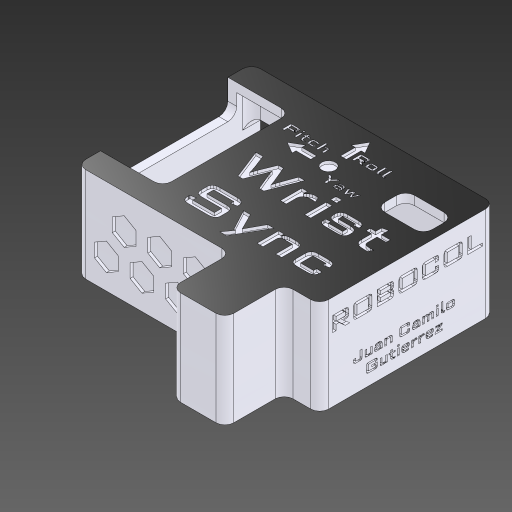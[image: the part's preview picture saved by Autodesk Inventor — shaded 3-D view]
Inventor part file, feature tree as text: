
AUTODESK INVENTOR PART (.ipt)
format: ipt  version: 2023.3 (Build 273359000, 359)  size: 2,437,120 bytes
history: native  units: mm
features: sketch x25, extrude x24, fillet x5, projected_geometry x3, other x2, plane x1, hole x1
ambient origin geometry x8: Origin, YZ Plane, XZ Plane, XY Plane, X Axis, Y Axis, Z Axis, Center Point
bodies: Solid1 (feature_tree)
feature tree (61):
  extrude  "Extrusion1"  Depth=60.0mm
  sketch  "Sketch2"  dims[d2=15.0mm d3=0.0mm d4=8.0mm]
  plane  "Work Plane1"
  extrude  "Extrusion2"  Depth=15.0mm
  extrude  "Extrusion3"  Depth=5.0mm
  extrude  "Extrusion4"  Depth=5.0mm
  extrude  "Extrusion5"  Depth=15.0mm
  extrude  "Extrusion6"  Depth=25.0mm
  extrude  "Extrusion7"  Depth=20.0mm
  extrude  "Extrusion8"  Depth=5.0mm
  hole  "Hole1"  [1 undecoded]
  extrude  "Extrusion9"  Depth=36.0mm
  extrude  "Extrusion10"  Depth=3.0mm TaperAngle=0.0deg
  extrude  "Extrusion11"  Depth=4.0mm
  extrude  "Extrusion12"  Depth=3.0mm TaperAngle=0.0deg
  extrude  "Extrusion13"  Depth=5.0mm
  extrude  "Extrusion14"  Depth=5.0mm
  extrude  "Extrusion15"  Depth=3.0mm TaperAngle=0.0deg
  extrude  "Extrusion16"  Depth=6.0mm
  extrude  "Extrusion17"  Depth=3.0mm TaperAngle=0.0deg
  fillet  "Fillet1"  Radius=12.0mm
  fillet  "Fillet2"  Radius=3.0mm
  fillet  "Fillet3"  Radius=17.0mm
  fillet  "Fillet4"  Radius=3.0mm
  fillet  "Fillet5"  Radius=3.0mm
  extrude  "Extrusion18"  Depth=9.0mm TaperAngle=0.0deg
  extrude  "Extrusion19"  Depth=5.0mm
  extrude  "Extrusion20"  Depth=10.0mm TaperAngle=0.0deg
  extrude  "Extrusion21"  Depth=10.0mm
  extrude  "Extrusion22"  Depth=10.0mm
  extrude  "Extrusion23"  Depth=5.0mm
  extrude  "Extrusion24"  Depth=3.0mm TaperAngle=0.0deg
  sketch  "Sketch1"  dims[d0=60.0mm d1=40.0mm]
  other  "Case"
  sketch  "Sketch3"  dims[d5=5.0mm d6=8.0mm]
  sketch  "Sketch4"  dims[d7=8.0mm d8=3.0mm d9=0.0mm d10=5.0mm]
  sketch  "Sketch5"  dims[d11=10.0mm d12=15.0mm]
  sketch  "Sketch6"  dims[d13=3.0mm d14=0.0mm d15=25.0mm]
  sketch  "Sketch7"  dims[d16=20.0mm d17=9.0mm]
  sketch  "Sketch8"  dims[d18=5.0mm d19=0.0mm d20=8.0mm]
  sketch  "Sketch9"  dims[d21=3.0mm d22=0.0mm d23=3.0mm]
  sketch  "Sketch10"  dims[d24=4.0mm d25=36.0mm]
  sketch  "Sketch11"  dims[d26=1.5mm d27=3.0mm d28=0.0mm]
  sketch  "Sketch12"  dims[d30=9.5mm d31=4.0mm]
  sketch  "Sketch13"  dims[d32=3.0mm d33=0.0mm d34=3.0mm d35=0.0mm]
  projected_geometry  "Projected Loop1"
  sketch  "Sketch14"  dims[d36=5.0mm d37=5.0mm]
  projected_geometry  "Projected Loop2"
  sketch  "Sketch15"  dims[d38=5.0mm d39=5.0mm]
  sketch  "Sketch16"  dims[d40=3.2mm d41=6.0mm d42=4.0mm d43=2.0mm d44=90.0deg d45=8.0mm d46=20.594885mm d47=3.0mm d48=0.0mm]
  sketch  "Sketch17"  dims[d49=12.0mm d50=6.0mm]
  projected_geometry  "Projected Loop3"
  sketch  "Sketch18"  dims[d52=4.0mm d53=25.25mm d54=0.0mm d55=12.0mm d56=3.0mm d57=17.0mm d58=3.0mm d59=3.0mm]
  sketch  "Sketch19"  dims[d60=25.25mm d61=0.0mm d62=9.0mm d63=0.0mm]
  sketch  "Sketch20"  dims[d64=3.0mm d65=0.0mm d67=5.0mm]
  sketch  "Sketch21"  dims[d69=8.0mm d70=10.0mm d71=0.0mm]
  sketch  "Sketch22"  dims[d72=9.0mm d73=10.0mm]
  sketch  "Sketch23"  dims[d74=3.0mm d75=0.0mm d76=10.0mm]
  sketch  "Sketch24"  dims[d77=5.0mm d78=8.0mm]
  sketch  "Sketch25"  dims[d79=3.0mm d80=3.0mm d81=0.0mm d82=3.0mm d83=0.0mm d84=3.0mm d85=3.0mm d86=3.0mm d87=3.0mm d88=3.0mm d89=1.0mm d90=0.0mm d91=8.0mm d92=10.0mm d93=10.0mm d94=30.0mm d96=12.0mm d97=20.0mm d99=12.0mm d102=1.0mm d103=0.0mm d104=1.0mm d105=0.0mm d106=2.0mm d107=5.0mm d108=60.0deg d109=60.0deg d110=4.0mm d111=4.0mm d112=4.619mm d113=1.0mm d114=1.0mm d115=17.0mm d116=22.0mm d117=10.0mm d118=1.0mm d119=0.0mm d120=1.0mm d121=0.0mm d122=1.0mm d123=0.0mm d137=1.5mm d138=5.0mm d140=30.0mm d142=1.625mm d143=1.625mm d144=1.625mm d145=1.625mm d146=1.625mm d147=1.0mm d148=0.0mm]
  other  "Image1"
note: 1 required parameter value undecoded (feature->parameter linkage not recoverable at this tier; creation-order binding heuristic only, values carry confidence <= 0.55)
